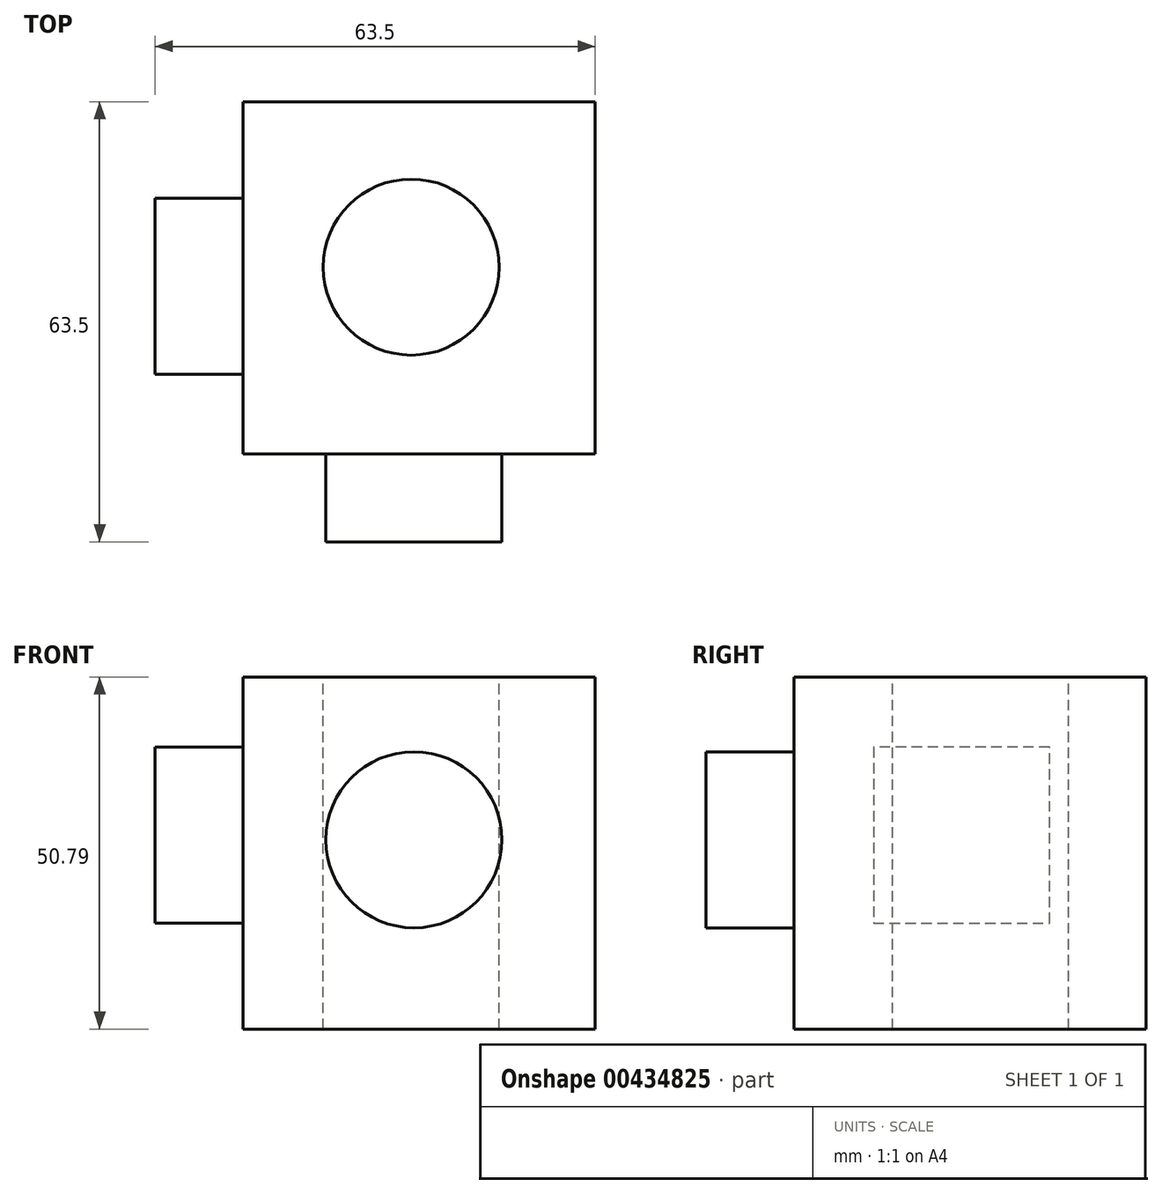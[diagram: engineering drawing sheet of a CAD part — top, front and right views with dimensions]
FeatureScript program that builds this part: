
annotation { "Feature Type Name" : "Feature", "Feature Type Description" : "" }
export const myFeature = defineFeature(function(context is Context, id is Id, definition is map)
    precondition{}
    {
        {
            var Q0;
            Q0=qCreatedBy(makeId("Front.planeOp"),FACE);
            var sketch = newSketch(context, id + "F0", { "sketchPlane" : qUnion([Q0])});
            skLineSegment(sketch, "E0", {"start": v(0, 0) * mm, "end": v(-50.8, 0) * mm});
            skLineSegment(sketch, "E1", {"start": v(-50.8, 0) * mm, "end": v(-50.8, 50.8) * mm});
            skLineSegment(sketch, "E2", {"start": v(-50.8, 50.8) * mm, "end": v(0, 50.8) * mm});
            skLineSegment(sketch, "E3", {"start": v(0, 50.8) * mm, "end": v(0, 0) * mm});
            skSolve(sketch);
        }
        {
            var Q0;
            Q0 = qSketchRegion(id + "F0", true);
            extrude(context, id + "F1", {"entities" : qUnion([Q0]), "depth" : 50.8 * mm});
        }
        {
            var Q0;
            Q0=makeQuery(id+"F1.opExtrude","CAP_FACE",FACE,{"disambiguationData":[OSD([sQuery(id+"F0.wireOp",EDGE,"E0"),sQuery(id+"F0.wireOp",EDGE,"E1"),sQuery(id+"F0.wireOp",EDGE,"E2"),sQuery(id+"F0.wireOp",EDGE,"E3")])],"isStart":false});
            var sketch = newSketch(context, id + "F2", { "sketchPlane" : qUnion([Q0])});
            skCircle(sketch, "E4", {"center": v(-26.16, 27.3) * mm, "radius": 12.7 * mm});
            skSolve(sketch);
        }
        {
            var Q0;
            Q0 = qSketchRegion(id + "F2", true);
            extrude(context, id + "F3", {"entities" : qUnion([Q0]), "operationType" : NewBodyOperationType.ADD, "depth" : 12.7 * mm});
        }
        {
            var Q0;
            Q0=makeQuery(id+"F1.opExtrude","SWEPT_FACE",FACE,{"disambiguationData":[OSD([sQuery(id+"F0.wireOp",EDGE,"E1")])]});
            var sketch = newSketch(context, id + "F4", { "sketchPlane" : qUnion([Q0])});
            skLineSegment(sketch, "E5", {"start": v(13.94, 15.28) * mm, "end": v(13.94, 40.68) * mm});
            skLineSegment(sketch, "E6", {"start": v(13.94, 40.68) * mm, "end": v(39.34, 40.68) * mm});
            skLineSegment(sketch, "E7", {"start": v(39.34, 40.68) * mm, "end": v(39.34, 15.28) * mm});
            skLineSegment(sketch, "E8", {"start": v(39.34, 15.28) * mm, "end": v(13.94, 15.28) * mm});
            skSolve(sketch);
        }
        {
            var Q0;
            Q0 = qSketchRegion(id + "F4", true);
            extrude(context, id + "F5", {"entities" : qUnion([Q0]), "operationType" : NewBodyOperationType.ADD, "depth" : 12.7 * mm});
        }
        {
            var Q0;
            Q0=makeQuery(id+"F1.opExtrude","SWEPT_FACE",FACE,{"disambiguationData":[OSD([sQuery(id+"F0.wireOp",EDGE,"E2")])]});
            var sketch = newSketch(context, id + "F6", { "sketchPlane" : qUnion([Q0])});
            skCircle(sketch, "E9", {"center": v(-26.55, -23.87) * mm, "radius": 12.7 * mm});
            skSolve(sketch);
        }
        {
            var Q0;
            Q0 = qSketchRegion(id + "F6", true);
            extrude(context, id + "F7", {"entities" : qUnion([Q0]), "operationType" : NewBodyOperationType.REMOVE, "oppositeDirection" : true, "depth" : 50.8 * mm});
        }
    });
